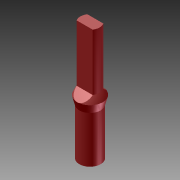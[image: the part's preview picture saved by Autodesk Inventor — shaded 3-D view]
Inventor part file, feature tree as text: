
AUTODESK INVENTOR PART (.ipt)
format: ipt  version: 2011 SP1 (Build 150282100, 282)  size: 98,304 bytes
history: native  units: in
note: dims shown in document units (in); Inventor stores cm internally (conversion verified against a paired STEP export)
features: other x7, sketch x2, revolve x1, extrude x1
ambient origin geometry x8: Origin, YZ Plane, XZ Plane, XY Plane, X Axis, Y Axis, Z Axis, Center Point
bodies: Solid1 (feature_tree)
feature tree (11):
  revolve  "Revolution1"  [1 undecoded]
  extrude  "Extrusion1"  [1 undecoded]
  other  "toggle17_5_to_body_XY"
  other  "toggle17_5_to_body_YZ"
  other  "toggle17_5_to_body_ZX"
  other  "toggle17_5_to_body_X"
  other  "toggle17_5_to_body_Y"
  other  "toggle17_5_to_body_Z"
  other  "toggle17_5_to_body_Center"
  sketch  "Sketch_1"  dims[d0=360.0deg d1=0.2in d2=0.0in]
  sketch  "Sketch_2"
note: 2 required parameter values undecoded (feature->parameter linkage not recoverable at this tier; creation-order binding heuristic only, values carry confidence <= 0.55)